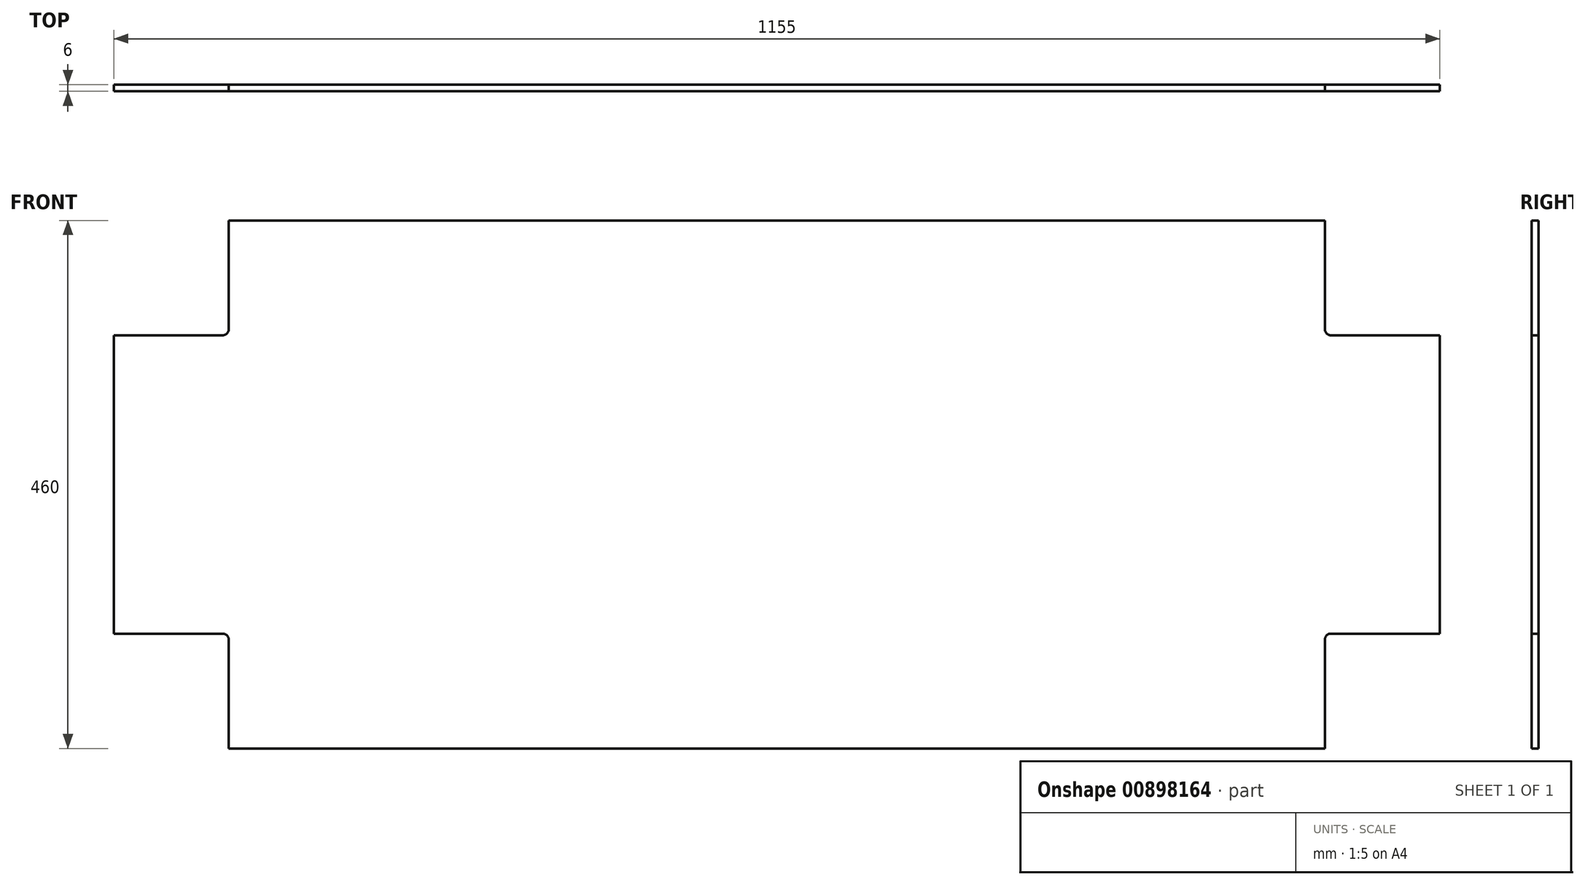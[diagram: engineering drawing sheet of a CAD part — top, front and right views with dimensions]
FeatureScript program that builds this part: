
annotation { "Feature Type Name" : "Feature", "Feature Type Description" : "" }
export const myFeature = defineFeature(function(context is Context, id is Id, definition is map)
    precondition{}
    {
        {
            var Q0;
            Q0=qCreatedBy(makeId("Front.planeOp"),FACE);
            var sketch = newSketch(context, id + "F0", { "sketchPlane" : qUnion([Q0])});
            skLineSegment(sketch, "E0.bottom", {"start": v(20, 286.06) * mm, "end": v(1175, 286.06) * mm});
            skLineSegment(sketch, "E0.top", {"start": v(20, -173.94) * mm, "end": v(1175, -173.94) * mm});
            skLineSegment(sketch, "E0.left", {"start": v(20, 286.06) * mm, "end": v(20, -173.94) * mm});
            skLineSegment(sketch, "E0.right", {"start": v(1175, 286.06) * mm, "end": v(1175, -173.94) * mm});
            skSolve(sketch);
        }
        {
            var Q0;
            Q0 = qSketchRegion(id + "F0", true);
            extrude(context, id + "F1", {"entities" : qUnion([Q0]), "depth" : 6 * mm, "offsetDistance" : 25 * mm});
        }
        {
            var Q0;
            Q0=makeQuery(id+"F1.opExtrude","CAP_FACE",FACE,{"disambiguationData":[OSD([sQuery(id+"F0.wireOp",EDGE,"E0.bottom"),sQuery(id+"F0.wireOp",EDGE,"E0.top"),sQuery(id+"F0.wireOp",EDGE,"E0.left"),sQuery(id+"F0.wireOp",EDGE,"E0.right")])],"isStart":false});
            var sketch = newSketch(context, id + "F2", { "sketchPlane" : qUnion([Q0])});
            skLineSegment(sketch, "E1.bottom", {"start": v(20, 286.06) * mm, "end": v(120, 286.06) * mm});
            skLineSegment(sketch, "E1.top", {"start": v(20, 186.06) * mm, "end": v(120, 186.06) * mm});
            skLineSegment(sketch, "E1.left", {"start": v(20, 286.06) * mm, "end": v(20, 186.06) * mm});
            skLineSegment(sketch, "E1.right", {"start": v(120, 286.06) * mm, "end": v(120, 186.06) * mm});
            skLineSegment(sketch, "E2.bottom", {"start": v(1175, -173.94) * mm, "end": v(1075, -173.94) * mm});
            skLineSegment(sketch, "E2.top", {"start": v(1175, -73.94) * mm, "end": v(1075, -73.94) * mm});
            skLineSegment(sketch, "E2.left", {"start": v(1175, -173.94) * mm, "end": v(1175, -73.94) * mm});
            skLineSegment(sketch, "E2.right", {"start": v(1075, -173.94) * mm, "end": v(1075, -73.94) * mm});
            skLineSegment(sketch, "E3.bottom", {"start": v(1175, 286.06) * mm, "end": v(1075, 286.06) * mm});
            skLineSegment(sketch, "E3.top", {"start": v(1175, 186.06) * mm, "end": v(1075, 186.06) * mm});
            skLineSegment(sketch, "E3.left", {"start": v(1175, 286.06) * mm, "end": v(1175, 186.06) * mm});
            skLineSegment(sketch, "E3.right", {"start": v(1075, 286.06) * mm, "end": v(1075, 186.06) * mm});
            skLineSegment(sketch, "E4.bottom", {"start": v(20, -173.94) * mm, "end": v(120, -173.94) * mm});
            skLineSegment(sketch, "E4.top", {"start": v(20, -73.94) * mm, "end": v(120, -73.94) * mm});
            skLineSegment(sketch, "E4.left", {"start": v(20, -173.94) * mm, "end": v(20, -73.94) * mm});
            skLineSegment(sketch, "E4.right", {"start": v(120, -173.94) * mm, "end": v(120, -73.94) * mm});
            skSolve(sketch);
        }
        {
            var Q0;
            Q0 = qSketchRegion(id + "F2", true);
            extrude(context, id + "F3", {"entities" : qUnion([Q0]), "operationType" : NewBodyOperationType.REMOVE, "oppositeDirection" : true, "depth" : 6 * mm, "offsetDistance" : 25 * mm});
        }
        {
            var Q0;
            Q0=makeQuery(id+"F3.boolean.opBoolean","COPY",EDGE,{"derivedFrom":makeQuery(id+"F3.opExtrude","SWEPT_EDGE",EDGE,{"disambiguationData":[OSD([sQuery(id+"F0.wireOp",EDGE,"E0.bottom"),sQuery(id+"F2.wireOp",EDGE,"E1.bottom"),sQuery(id+"F2.wireOp",EDGE,"E1.right")])]})});
            var Q1;
            Q1=makeQuery(id+"F3.boolean.opBoolean","COPY",EDGE,{"derivedFrom":makeQuery(id+"F3.opExtrude","SWEPT_EDGE",EDGE,{"disambiguationData":[OSD([sQuery(id+"F2.wireOp",EDGE,"E1.top"),sQuery(id+"F2.wireOp",EDGE,"E1.right")])]})});
            var Q2;
            Q2=makeQuery(id+"F3.boolean.opBoolean","COPY",EDGE,{"derivedFrom":makeQuery(id+"F3.opExtrude","SWEPT_EDGE",EDGE,{"disambiguationData":[OSD([sQuery(id+"F0.wireOp",EDGE,"E0.left"),sQuery(id+"F2.wireOp",EDGE,"E1.top"),sQuery(id+"F2.wireOp",EDGE,"E1.left")])]})});
            var Q3;
            Q3=makeQuery(id+"F3.boolean.opBoolean","COPY",EDGE,{"derivedFrom":makeQuery(id+"F3.opExtrude","SWEPT_EDGE",EDGE,{"disambiguationData":[OSD([sQuery(id+"F0.wireOp",EDGE,"E0.left"),sQuery(id+"F2.wireOp",EDGE,"E4.top"),sQuery(id+"F2.wireOp",EDGE,"E4.left")])]})});
            var Q4;
            Q4=makeQuery(id+"F3.boolean.opBoolean","COPY",EDGE,{"derivedFrom":makeQuery(id+"F3.opExtrude","SWEPT_EDGE",EDGE,{"disambiguationData":[OSD([sQuery(id+"F2.wireOp",EDGE,"E4.top"),sQuery(id+"F2.wireOp",EDGE,"E4.right")])]})});
            var Q5;
            Q5=makeQuery(id+"F3.boolean.opBoolean","COPY",EDGE,{"derivedFrom":makeQuery(id+"F3.opExtrude","SWEPT_EDGE",EDGE,{"disambiguationData":[OSD([sQuery(id+"F0.wireOp",EDGE,"E0.top"),sQuery(id+"F2.wireOp",EDGE,"E4.bottom"),sQuery(id+"F2.wireOp",EDGE,"E4.right")])]})});
            var Q6;
            Q6=makeQuery(id+"F3.boolean.opBoolean","COPY",EDGE,{"derivedFrom":makeQuery(id+"F3.opExtrude","SWEPT_EDGE",EDGE,{"disambiguationData":[OSD([sQuery(id+"F0.wireOp",EDGE,"E0.top"),sQuery(id+"F2.wireOp",EDGE,"E2.bottom"),sQuery(id+"F2.wireOp",EDGE,"E2.right")])]})});
            var Q7;
            Q7=makeQuery(id+"F3.boolean.opBoolean","COPY",EDGE,{"derivedFrom":makeQuery(id+"F3.opExtrude","SWEPT_EDGE",EDGE,{"disambiguationData":[OSD([sQuery(id+"F2.wireOp",EDGE,"E2.top"),sQuery(id+"F2.wireOp",EDGE,"E2.right")])]})});
            var Q8;
            Q8=makeQuery(id+"F3.boolean.opBoolean","COPY",EDGE,{"derivedFrom":makeQuery(id+"F3.opExtrude","SWEPT_EDGE",EDGE,{"disambiguationData":[OSD([sQuery(id+"F0.wireOp",EDGE,"E0.right"),sQuery(id+"F2.wireOp",EDGE,"E2.top"),sQuery(id+"F2.wireOp",EDGE,"E2.left")])]})});
            var Q9;
            Q9=makeQuery(id+"F3.boolean.opBoolean","COPY",EDGE,{"derivedFrom":makeQuery(id+"F3.opExtrude","SWEPT_EDGE",EDGE,{"disambiguationData":[OSD([sQuery(id+"F0.wireOp",EDGE,"E0.right"),sQuery(id+"F2.wireOp",EDGE,"E3.top"),sQuery(id+"F2.wireOp",EDGE,"E3.left")])]})});
            var Q10;
            Q10=makeQuery(id+"F3.boolean.opBoolean","COPY",EDGE,{"derivedFrom":makeQuery(id+"F3.opExtrude","SWEPT_EDGE",EDGE,{"disambiguationData":[OSD([sQuery(id+"F2.wireOp",EDGE,"E3.top"),sQuery(id+"F2.wireOp",EDGE,"E3.right")])]})});
            var Q11;
            Q11=makeQuery(id+"F3.boolean.opBoolean","COPY",EDGE,{"derivedFrom":makeQuery(id+"F3.opExtrude","SWEPT_EDGE",EDGE,{"disambiguationData":[OSD([sQuery(id+"F0.wireOp",EDGE,"E0.bottom"),sQuery(id+"F2.wireOp",EDGE,"E3.bottom"),sQuery(id+"F2.wireOp",EDGE,"E3.right")])]})});
            fillet(context, id + "F4", {"entities" : qUnion([Q0, Q1, Q2, Q3, Q4, Q5, Q6, Q7, Q8, Q9, Q10, Q11]), "radius" : 5 * mm, "tangentPropagation" : true, "allowEdgeOverflow" : false});
        }
    });
